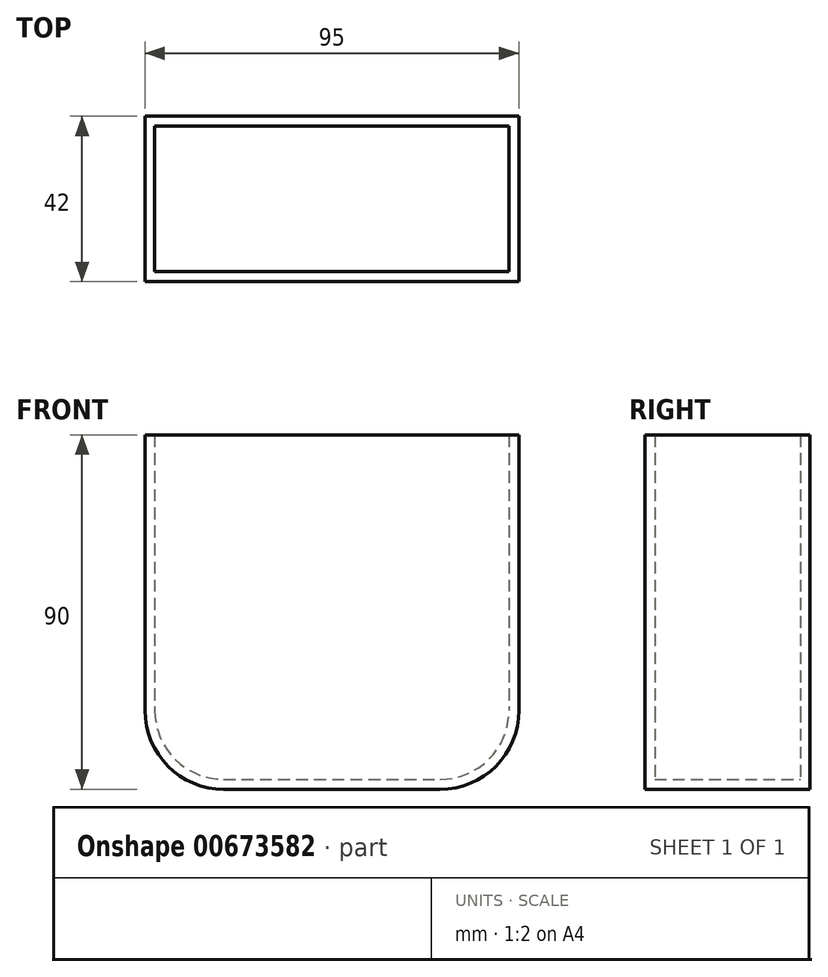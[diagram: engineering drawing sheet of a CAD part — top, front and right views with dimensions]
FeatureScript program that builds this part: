
annotation { "Feature Type Name" : "Feature", "Feature Type Description" : "" }
export const myFeature = defineFeature(function(context is Context, id is Id, definition is map)
    precondition{}
    {
        {
            var Q0;
            Q0=qCreatedBy(makeId("Front.planeOp"),FACE);
            var sketch = newSketch(context, id + "F0", { "sketchPlane" : qUnion([Q0])});
            skLineSegment(sketch, "E0.bottom", {"start": v(0, 0) * mm, "end": v(95, 0) * mm});
            skLineSegment(sketch, "E0.top", {"start": v(20, -90) * mm, "end": v(75, -90) * mm});
            skLineSegment(sketch, "E0.left", {"start": v(0, 0) * mm, "end": v(0, -70) * mm});
            skLineSegment(sketch, "E0.right", {"start": v(95, 0) * mm, "end": v(95, -70) * mm});
            skPoint(sketch, "E1.visualSharp", {"position": v(0, -90) * mm});
            skArc(sketch, "E1.filletArc", {"start": v(0, -70) * mm, "mid": v(5.86, -84.14) * mm, "end": v(20, -90) * mm});
            skPoint(sketch, "E2.visualSharp", {"position": v(95, -90) * mm});
            skArc(sketch, "E2.filletArc", {"start": v(75, -90) * mm, "mid": v(89.14, -84.14) * mm, "end": v(95, -70) * mm});
            skSolve(sketch);
        }
        {
            var Q0;
            Q0 = qSketchRegion(id + "F0", true);
            extrude(context, id + "F1", {"entities" : qUnion([Q0]), "depth" : 42 * mm, "offsetDistance" : 25 * mm});
        }
        {
            var Q0;
            Q0=makeQuery(id+"F1.opExtrude","SWEPT_FACE",FACE,{"disambiguationData":[OSD([sQuery(id+"F0.wireOp",EDGE,"E0.bottom")])]});
            shell(context, id + "F2", {"entities" : qUnion([Q0]), "thickness" : 2.5 * mm});
        }
    });
